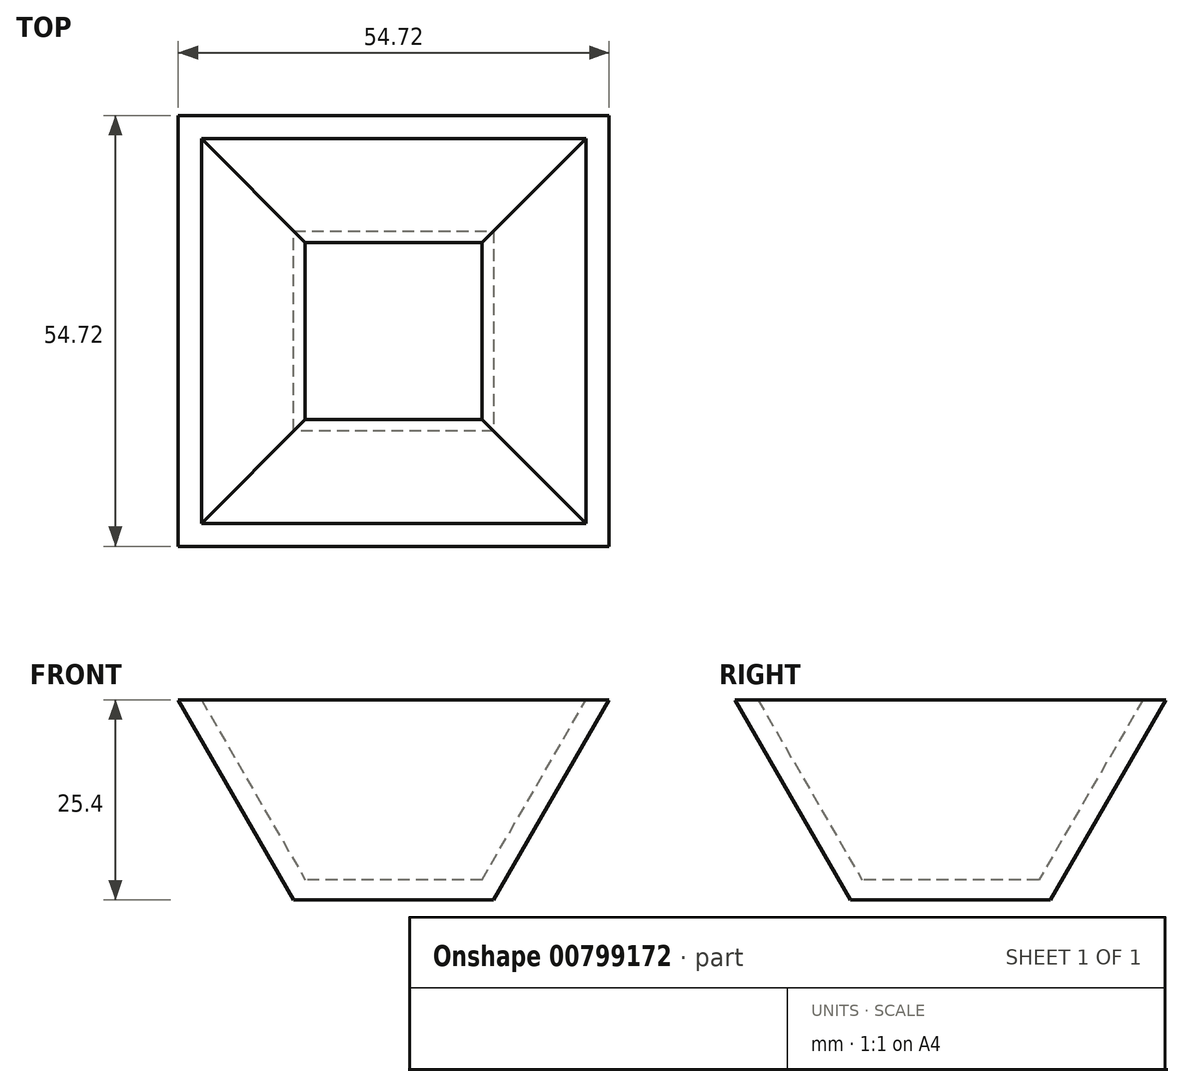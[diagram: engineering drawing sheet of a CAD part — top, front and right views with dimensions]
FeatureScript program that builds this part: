
annotation { "Feature Type Name" : "Feature", "Feature Type Description" : "" }
export const myFeature = defineFeature(function(context is Context, id is Id, definition is map)
    precondition{}
    {
        {
            var Q0;
            Q0=qCreatedBy(makeId("Top.planeOp"),FACE);
            var sketch = newSketch(context, id + "F0", { "sketchPlane" : qUnion([Q0])});
            skLineSegment(sketch, "E0.bottom", {"start": v(12.7, -12.7) * mm, "end": v(-12.7, -12.7) * mm});
            skLineSegment(sketch, "E0.top", {"start": v(12.7, 12.7) * mm, "end": v(-12.7, 12.7) * mm});
            skLineSegment(sketch, "E0.left", {"start": v(12.7, -12.7) * mm, "end": v(12.7, 12.7) * mm});
            skLineSegment(sketch, "E0.right", {"start": v(-12.7, -12.7) * mm, "end": v(-12.7, 12.7) * mm});
            skPoint(sketch, "E0.middle", {"position": v(0, 0) * mm});
            skSolve(sketch);
        }
        {
            var Q0;
            Q0=qSketchRegion(id+"F0",true);
            extrude(context, id + "F1", {"entities" : qUnion([Q0]), "depth" : 25.4 * mm, "hasDraft" : true, "draftAngle" : 30 * degree});
        }
        {
            var Q0;
            Q0=makeQuery(id+"F1.opExtrude","CAP_FACE",FACE,{"disambiguationData":[OSD([sQuery(id+"F0.wireOp",EDGE,"E0.bottom"),sQuery(id+"F0.wireOp",EDGE,"E0.top"),sQuery(id+"F0.wireOp",EDGE,"E0.left"),sQuery(id+"F0.wireOp",EDGE,"E0.right")])],"isStart":false});
            shell(context, id + "F2", {"entities" : qUnion([Q0]), "thickness" : 2.54 * mm});
        }
    });
